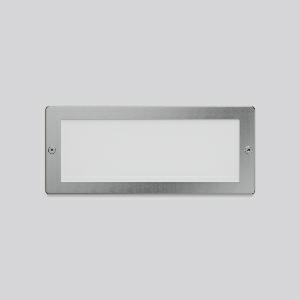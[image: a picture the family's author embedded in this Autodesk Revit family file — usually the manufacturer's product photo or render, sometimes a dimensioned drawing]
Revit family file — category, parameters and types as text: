
# Revit family: brick_steps_641307_000_1_76_7ea7
name_source: partatom
category: Lighting Fixtures
units: mm (PartAtom-declared; Revit-internal decimal feet)

## family parameters
Cut with Voids When Loaded = No
Host = Face
Light Source = No
Part Type = Normal
Room Calculation Point = No
Round Connector Dimension = Use Diameter
Shared = No

## types (1)
- BRICK STEPS (1 x LED Modul 840, 200 lm, 4000)
    Apparent Load = 6 VA
    CIE Flux Codes = 13 37 67 50 100
    Color Rendering = 80
    Color Temperature = 4000
    Default Elevation = 1800 mm
    Description = Series: BRICK STEPS
Robust LED wall and step luminaires. Housing: die-cast aluminium, powder-coated. Shock resistant plastic (polycarbonate) cover, opal, with stainless steel frame. Driver integrated. With second cable entry for loop through. Recommended accessory: recessed support. 
Colour: stainless steel
Length: 236 mm
Width: 100 mm
Height: 5 mm
Lamp: LED
System power: 6 W
Rated luminous flux: 200 lm
Luminous efficiency: 33 lm/W
Control gear: Converter, dimmable, DALI
Protection class: I
Type of protection: IP 66
    Height = 5 mm  [stored 0.0164042 ft]
    Lamp = 1 x LED Modul 840
    Lamp Light Flux = 200 lm
    Lamp count = 1
    Length = 236 mm
    Lifetime = 50000 h
    Luminous efficacy = 33 lm/W
    Manufacturer = RZB
    ModVariant = No
    Model = 641307.000.1.76
    Mounting Place = Wall
    Mounting Type = Recessed
    Number of Poles = 1
    OnlyDefault = Yes
    Power Factor = 1
    Product Name = BRICK STEPS
    Product group = Recessed wall luminaires
    ProductGroupID = 2004
    Protection Class = Protection class I
    Protection Degree = IP 66
    RLX_Detail_Level = 1
    RLX_Emergency_Light_Flux = 0 lm
    RLX_Emergency_Type = 0
    RLX_Emergency_Type_DB = No
    RlxData = <blob elided: 35821 chars, md5=d13d10a6>
    Socket = socket
    Standby Power = 0 W
    System Light Flux = 200 lm
    System Power = 6 W
    Type Comments = Product without accessories
    Type Image = 641307.000.jpg
    URL = http://relux.com
    VarID = ---
    Voltage = 230 V
    Voltage Range = 220-240 V
    Weight = 0.00 kg
    Width = 100 mm  [stored 0.328084 ft]

note: [stored X ft] marks values corroborated as IEEE doubles in the binary element streams (Revit-internal decimal feet)

## geometry (parser evidence)
native form markers: Blend x4, Sweep x10
no freeform markers — native parametric forms only
